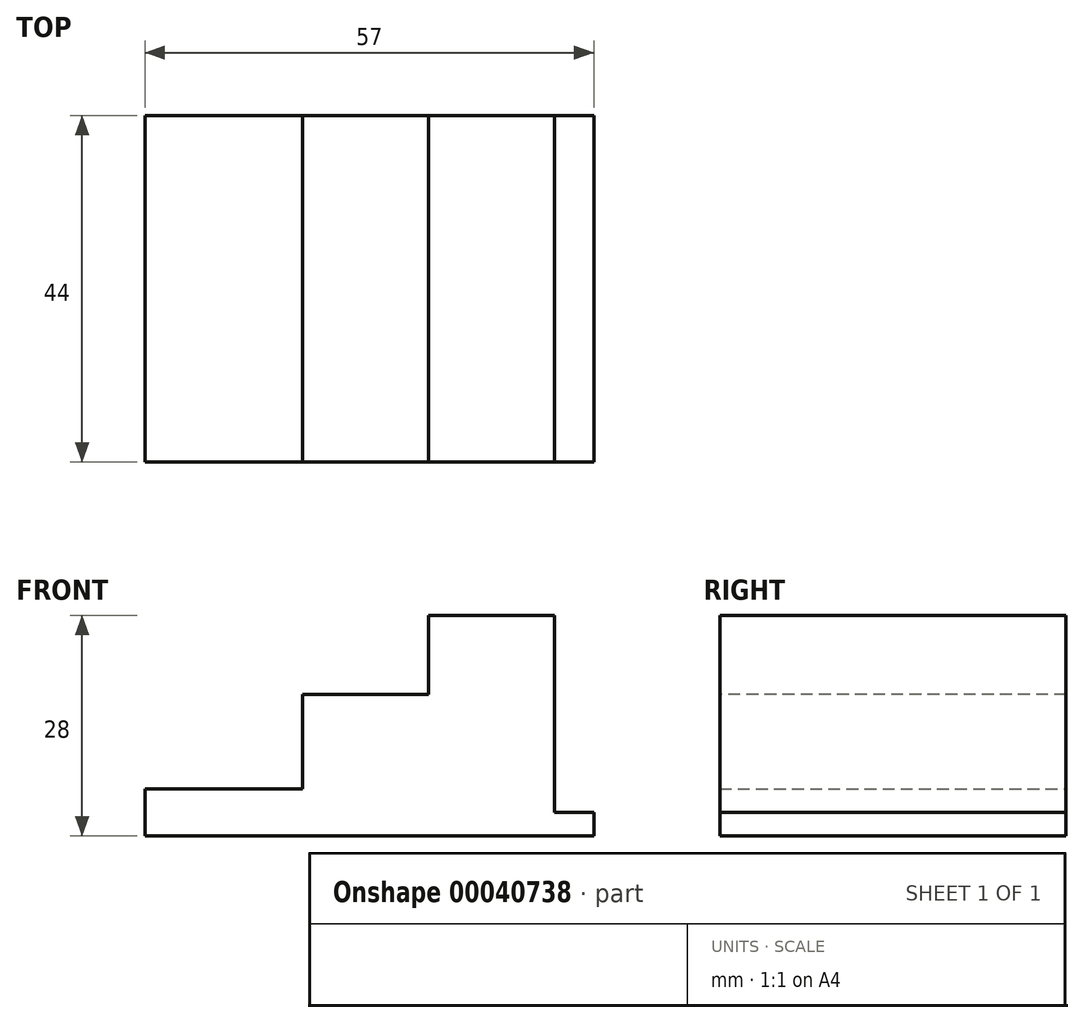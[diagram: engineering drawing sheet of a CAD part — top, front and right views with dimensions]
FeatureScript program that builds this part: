
annotation { "Feature Type Name" : "Feature", "Feature Type Description" : "" }
export const myFeature = defineFeature(function(context is Context, id is Id, definition is map)
    precondition{}
    {
        {
            var Q0;
            Q0=qCreatedBy(makeId("Top.planeOp"),FACE);
            var sketch = newSketch(context, id + "F0", { "sketchPlane" : qUnion([Q0])});
            skLineSegment(sketch, "E0.rect.bottom", {"start": v(28.5, -22) * mm, "end": v(-28.5, -22) * mm});
            skLineSegment(sketch, "E0.rect.top", {"start": v(28.5, 22) * mm, "end": v(-28.5, 22) * mm});
            skLineSegment(sketch, "E0.rect.left", {"start": v(28.5, -22) * mm, "end": v(28.5, 22) * mm});
            skLineSegment(sketch, "E0.rect.right", {"start": v(-28.5, -22) * mm, "end": v(-28.5, 22) * mm});
            skPoint(sketch, "E0.rect.middle", {"position": v(0, 0) * mm});
            skSolve(sketch);
        }
        {
            var Q0;
            Q0=makeQuery(id+"F0.imprint","IMPRINT",FACE,{"disambiguationData":[TD([[makeQuery(id+"F0.imprint","IMPRINT",EDGE,{"derivedFrom":sQuery(id+"F0.wireOp",EDGE,"E0.rect.bottom")}),-1.0]])]});
            extrude(context, id + "F1", {"entities" : qUnion([Q0]), "depth" : 28 * mm});
        }
        {
            var Q0;
            Q0=makeQuery(id+"F1.opExtrude","CAP_FACE",FACE,{"disambiguationData":[OSD([sQuery(id+"F0.wireOp",EDGE,"E0.rect.bottom"),sQuery(id+"F0.wireOp",EDGE,"E0.rect.top"),sQuery(id+"F0.wireOp",EDGE,"E0.rect.left"),sQuery(id+"F0.wireOp",EDGE,"E0.rect.right")])],"isStart":false});
            var sketch = newSketch(context, id + "F2", { "sketchPlane" : qUnion([Q0])});
            skLineSegment(sketch, "E1", {"start": v(-8.5, 22) * mm, "end": v(-8.5, -22) * mm});
            skSolve(sketch);
        }
        {
            var Q0;
            {var subQ1=sQuery(id+"F2.wireOp",EDGE,"E1");Q0=makeQuery(id+"F2.imprint","IMPRINT",FACE,{"disambiguationData":[TD([[makeQuery(id+"F2.imprint","IMPRINT",EDGE,{"derivedFrom":subQ1}),-1.0]])]});}
            extrude(context, id + "F3", {"entities" : qUnion([Q0]), "operationType" : NewBodyOperationType.REMOVE, "oppositeDirection" : true, "depth" : 22 * mm});
        }
        {
            var Q0;
            Q0=makeQuery(id+"F1.opExtrude","CAP_FACE",FACE,{"disambiguationData":[OSD([sQuery(id+"F0.wireOp",EDGE,"E0.rect.bottom"),sQuery(id+"F0.wireOp",EDGE,"E0.rect.top"),sQuery(id+"F0.wireOp",EDGE,"E0.rect.left"),sQuery(id+"F0.wireOp",EDGE,"E0.rect.right")])],"isStart":false});
            var sketch = newSketch(context, id + "F4", { "sketchPlane" : qUnion([Q0])});
            skLineSegment(sketch, "E2", {"start": v(7.5, 22) * mm, "end": v(7.5, -22) * mm});
            skSolve(sketch);
        }
        {
            var Q0;
            {var subQ1=sQuery(id+"F4.wireOp",EDGE,"E2");Q0=makeQuery(id+"F4.imprint","IMPRINT",FACE,{"disambiguationData":[TD([[makeQuery(id+"F4.imprint","IMPRINT",EDGE,{"derivedFrom":subQ1}),-1.0]])]});}
            extrude(context, id + "F5", {"entities" : qUnion([Q0]), "operationType" : NewBodyOperationType.REMOVE, "oppositeDirection" : true, "depth" : 10 * mm});
        }
        {
            var Q0;
            Q0=makeQuery(id+"F1.opExtrude","CAP_FACE",FACE,{"disambiguationData":[OSD([sQuery(id+"F0.wireOp",EDGE,"E0.rect.bottom"),sQuery(id+"F0.wireOp",EDGE,"E0.rect.top"),sQuery(id+"F0.wireOp",EDGE,"E0.rect.left"),sQuery(id+"F0.wireOp",EDGE,"E0.rect.right")])],"isStart":false});
            var sketch = newSketch(context, id + "F6", { "sketchPlane" : qUnion([Q0])});
            skLineSegment(sketch, "E3", {"start": v(23.5, 22) * mm, "end": v(23.5, -22) * mm});
            skSolve(sketch);
        }
        {
            var Q0;
            {var subQ1=sQuery(id+"F6.wireOp",EDGE,"E3");Q0=makeQuery(id+"F6.imprint","IMPRINT",FACE,{"disambiguationData":[TD([[makeQuery(id+"F6.imprint","IMPRINT",EDGE,{"derivedFrom":subQ1}),1.0]])]});}
            extrude(context, id + "F7", {"entities" : qUnion([Q0]), "operationType" : NewBodyOperationType.REMOVE, "oppositeDirection" : true, "depth" : 25 * mm});
        }
    });
